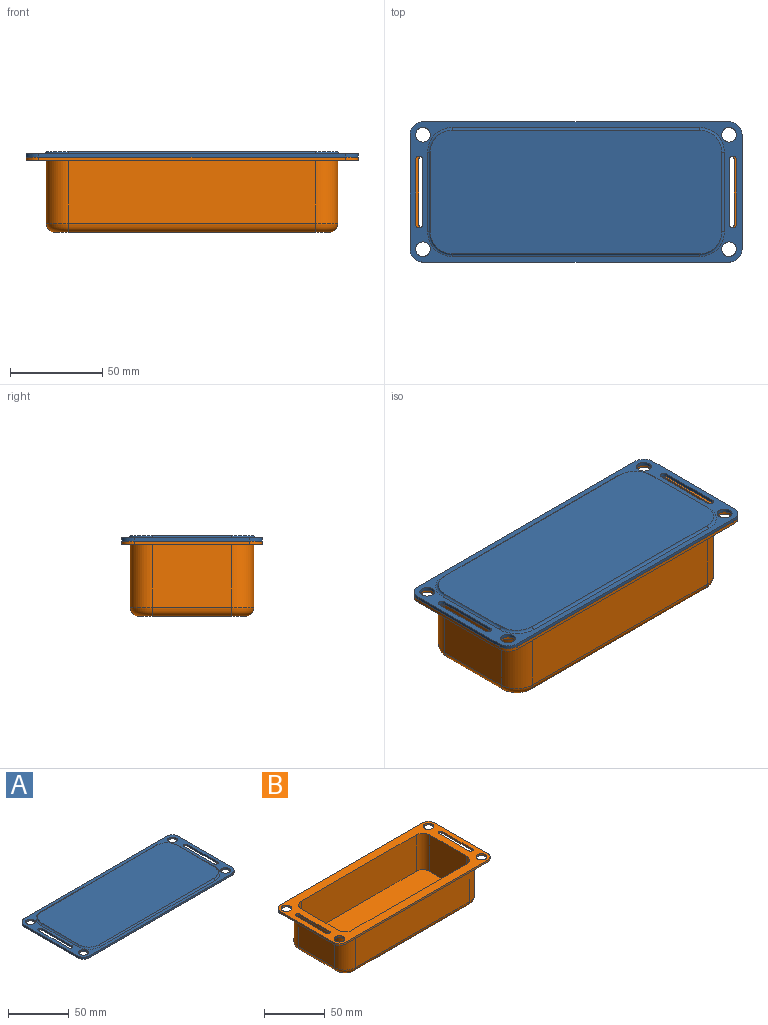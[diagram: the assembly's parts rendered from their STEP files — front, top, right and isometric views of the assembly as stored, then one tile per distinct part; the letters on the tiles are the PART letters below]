
ASSEMBLY  parts=2 mates=1
PART A: 31 faces, bbox 180x76x3.3 mm
  f0: plane 180x76mm, normal (0,0,1), area 2031.5mm2, adj f2,f3,f4,f5,f6,f7,f8,f9
  f1: plane 180x76mm, normal (0,0,-1), area 13131.7mm2, adj f2,f3,f4,f5,f6,f7,f8,f9
  f2: plane 62x1.8mm, normal (-1,0,0), area 111.6mm2, adj f0,f1,f3,f9
  f3: cylinder r=7mm len=7mm, axis (0,0,-1), area 19.8mm2, adj f0,f1,f2,f4
  f4: plane 166x1.8mm, normal (0,-1,0), area 298.8mm2, adj f0,f1,f3,f5
  f5: cylinder r=7mm len=7mm, axis (0,0,-1), area 19.8mm2, adj f0,f1,f4,f6
  f6: plane 62x1.8mm, normal (1,0,0), area 111.6mm2, adj f0,f1,f5,f7
  f7: cylinder r=7mm len=7mm, axis (0,0,-1), area 19.8mm2, adj f0,f1,f6,f8
  f8: plane 166x1.8mm, normal (0,1,0), area 298.8mm2, adj f0,f1,f7,f9
  f9: cylinder r=7mm len=7mm, axis (0,0,-1), area 19.8mm2, adj f0,f1,f2,f8
  f10: plane 158x67mm, normal (0,0,1), area 10462.4mm2, adj f11,f12,f13,f14,f15,f16,f17,f18
  f11: cylinder r=1.5mm len=43mm, axis (0,1,0), area 88.3mm2, adj f0,f10,f12,f13
  f12: torus R=13.47mm, axis (0,0,1), area 40.6mm2, adj f0,f10,f11,f14
  f13: torus R=13.47mm, axis (0,0,1), area 40.6mm2, adj f0,f10,f11,f15
  f14: cylinder r=1.5mm len=134mm, axis (-1,0,0), area 275.3mm2, adj f0,f10,f12,f16
  f15: cylinder r=1.5mm len=134mm, axis (-1,0,0), area 275.3mm2, adj f0,f10,f13,f17
  f16: torus R=13.47mm, axis (0,0,1), area 40.6mm2, adj f0,f10,f14,f18
  f17: torus R=13.47mm, axis (0,0,1), area 40.6mm2, adj f0,f10,f15,f18
  f18: cylinder r=1.5mm len=43mm, axis (0,1,0), area 88.3mm2, adj f0,f10,f16,f17
  f19: cylinder r=4mm len=8mm, axis (0,0,-1), area 45.2mm2, adj f0,f1
  f20: cylinder r=4mm len=8mm, axis (0,0,-1), area 45.2mm2, adj f0,f1
  f21: cylinder r=4mm len=8mm, axis (0,0,-1), area 45.2mm2, adj f0,f1
  f22: cylinder r=4mm len=8mm, axis (0,0,-1), area 45.2mm2, adj f0,f1
  f23: plane 35x1.8mm, normal (-1,0,0), area 63mm2, adj f0,f1,f24,f26
  f24: cylinder r=2mm len=4mm, axis (0,0,1), area 11.3mm2, adj f0,f1,f23,f25
  f25: plane 35x1.8mm, normal (1,0,0), area 63mm2, adj f0,f1,f24,f26
  f26: cylinder r=2mm len=4mm, axis (0,0,1), area 11.3mm2, adj f0,f1,f23,f25
  f27: plane 35x1.8mm, normal (1,0,0), area 63mm2, adj f0,f1,f28,f30
  f28: cylinder r=2mm len=4mm, axis (0,0,1), area 11.3mm2, adj f0,f1,f27,f29
  f29: plane 35x1.8mm, normal (-1,0,0), area 63mm2, adj f0,f1,f28,f30
  f30: cylinder r=2mm len=4mm, axis (0,0,1), area 11.3mm2, adj f0,f1,f27,f29
PART B: 48 faces, bbox 180x76x40.9 mm
  f0: plane 180x76mm, normal (0,0,-1), area 2615.9mm2, adj f1,f2,f3,f4,f5,f6,f7,f8
  f1: plane 62x1.8mm, normal (-1,0,0), area 111.6mm2, adj f0,f2,f8,f9
  f2: cylinder r=7mm len=7mm, axis (0,0,1), area 19.8mm2, adj f0,f1,f3,f9
  f3: plane 166x1.8mm, normal (0,-1,0), area 298.8mm2, adj f0,f2,f4,f9
  f4: cylinder r=7mm len=7mm, axis (0,0,1), area 19.8mm2, adj f0,f3,f5,f9
  f5: plane 62x1.8mm, normal (1,0,0), area 111.6mm2, adj f0,f4,f6,f9
  f6: cylinder r=7mm len=7mm, axis (0,0,1), area 19.8mm2, adj f0,f5,f7,f9
  f7: plane 166x1.8mm, normal (0,1,0), area 298.8mm2, adj f0,f6,f8,f9
  f8: cylinder r=7mm len=7mm, axis (0,0,1), area 19.8mm2, adj f0,f1,f7,f9
  f9: plane 180x76mm, normal (0,0,1), area 4283.3mm2, adj f1,f2,f3,f4,f5,f6,f7,f8
  f10: plane 43x34.1mm, normal (-1,0,0), area 1466.3mm2, adj f0,f11,f17,f32
  f11: cylinder r=12mm len=34.1mm, axis (0,0,1), area 642.8mm2, adj f0,f10,f12,f30
  f12: plane 134x34.1mm, normal (0,-1,0), area 4569.4mm2, adj f0,f11,f13,f28
  f13: cylinder r=12mm len=34.1mm, axis (0,0,1), area 642.8mm2, adj f0,f12,f14,f29
  f14: plane 43x34.1mm, normal (1,0,0), area 1466.3mm2, adj f0,f13,f15,f31
  f15: cylinder r=12mm len=34.1mm, axis (0,0,1), area 642.8mm2, adj f0,f14,f16,f33
  f16: plane 134x34.1mm, normal (0,1,0), area 4569.4mm2, adj f0,f15,f17,f35
  f17: cylinder r=12mm len=34.1mm, axis (0,0,1), area 642.8mm2, adj f0,f10,f16,f34
  f18: plane 148x57mm, normal (0,0,-1), area 8393.9mm2, adj f28,f29,f30,f31,f32,f33,f34,f35
  f19: cylinder r=8mm len=36.9mm, axis (0,0,1), area 463.7mm2, adj f9,f20,f26,f27
  f20: plane 134x36.9mm, normal (0,-1,0), area 4944.6mm2, adj f9,f19,f21,f27
  f21: cylinder r=8mm len=36.9mm, axis (0,0,1), area 463.7mm2, adj f9,f20,f22,f27
  f22: plane 43x36.9mm, normal (-1,0,0), area 1586.7mm2, adj f9,f21,f23,f27
  f23: cylinder r=8mm len=36.9mm, axis (0,0,1), area 463.7mm2, adj f9,f22,f24,f27
  f24: plane 134x36.9mm, normal (0,1,0), area 4944.6mm2, adj f9,f23,f25,f27
  f25: cylinder r=8mm len=36.9mm, axis (0,0,1), area 463.7mm2, adj f9,f24,f26,f27
  f26: plane 43x36.9mm, normal (1,0,0), area 1586.7mm2, adj f9,f19,f25,f27
  f27: plane 150x59mm, normal (0,0,1), area 8795.1mm2, adj f19,f20,f21,f22,f23,f24,f25,f26
  f28: cylinder r=5mm len=134mm, axis (-1,0,0), area 1052.4mm2, adj f12,f18,f29,f30
  f29: torus R=7mm, axis (0,0,1), area 125.6mm2, adj f13,f18,f28,f31
  f30: torus R=7mm, axis (0,0,1), area 125.6mm2, adj f11,f18,f28,f32
  f31: cylinder r=5mm len=43mm, axis (0,-1,0), area 337.7mm2, adj f14,f18,f29,f33
  f32: cylinder r=5mm len=43mm, axis (0,1,0), area 337.7mm2, adj f10,f18,f30,f34
  f33: torus R=7mm, axis (0,0,1), area 125.6mm2, adj f15,f18,f31,f35
  f34: torus R=7mm, axis (0,0,1), area 125.6mm2, adj f17,f18,f32,f35
  f35: cylinder r=5mm len=134mm, axis (1,0,0), area 1052.4mm2, adj f16,f18,f33,f34
  f36: cylinder r=4.5mm len=9mm, axis (0,0,1), area 50.9mm2, adj f0,f9
  f37: cylinder r=4.5mm len=9mm, axis (0,0,1), area 50.9mm2, adj f0,f9
  f38: cylinder r=4.5mm len=9mm, axis (0,0,1), area 50.9mm2, adj f0,f9
  f39: cylinder r=4.5mm len=9mm, axis (0,0,1), area 50.9mm2, adj f0,f9
  f40: plane 35x1.8mm, normal (-1,0,0), area 63mm2, adj f0,f9,f41,f43
  f41: cylinder r=2mm len=4mm, axis (0,0,1), area 11.3mm2, adj f0,f9,f40,f42
  f42: plane 35x1.8mm, normal (1,0,0), area 63mm2, adj f0,f9,f41,f43
  f43: cylinder r=2mm len=4mm, axis (0,0,1), area 11.3mm2, adj f0,f9,f40,f42
  f44: plane 35x1.8mm, normal (-1,0,0), area 63mm2, adj f0,f9,f45,f47
  f45: cylinder r=2mm len=4mm, axis (0,0,1), area 11.3mm2, adj f0,f9,f44,f46
  f46: plane 35x1.8mm, normal (1,0,0), area 63mm2, adj f0,f9,f45,f47
  f47: cylinder r=2mm len=4mm, axis (0,0,1), area 11.3mm2, adj f0,f9,f44,f46
PLACE A t=(-35.16,-29.84,6.14)mm
PLACE B t=(-35.16,-29.84,5.24)mm
MATE fastened A.f9 <-> B.f8  axis (0,0,-1) through (-118.16,1.16,6.14)mm
